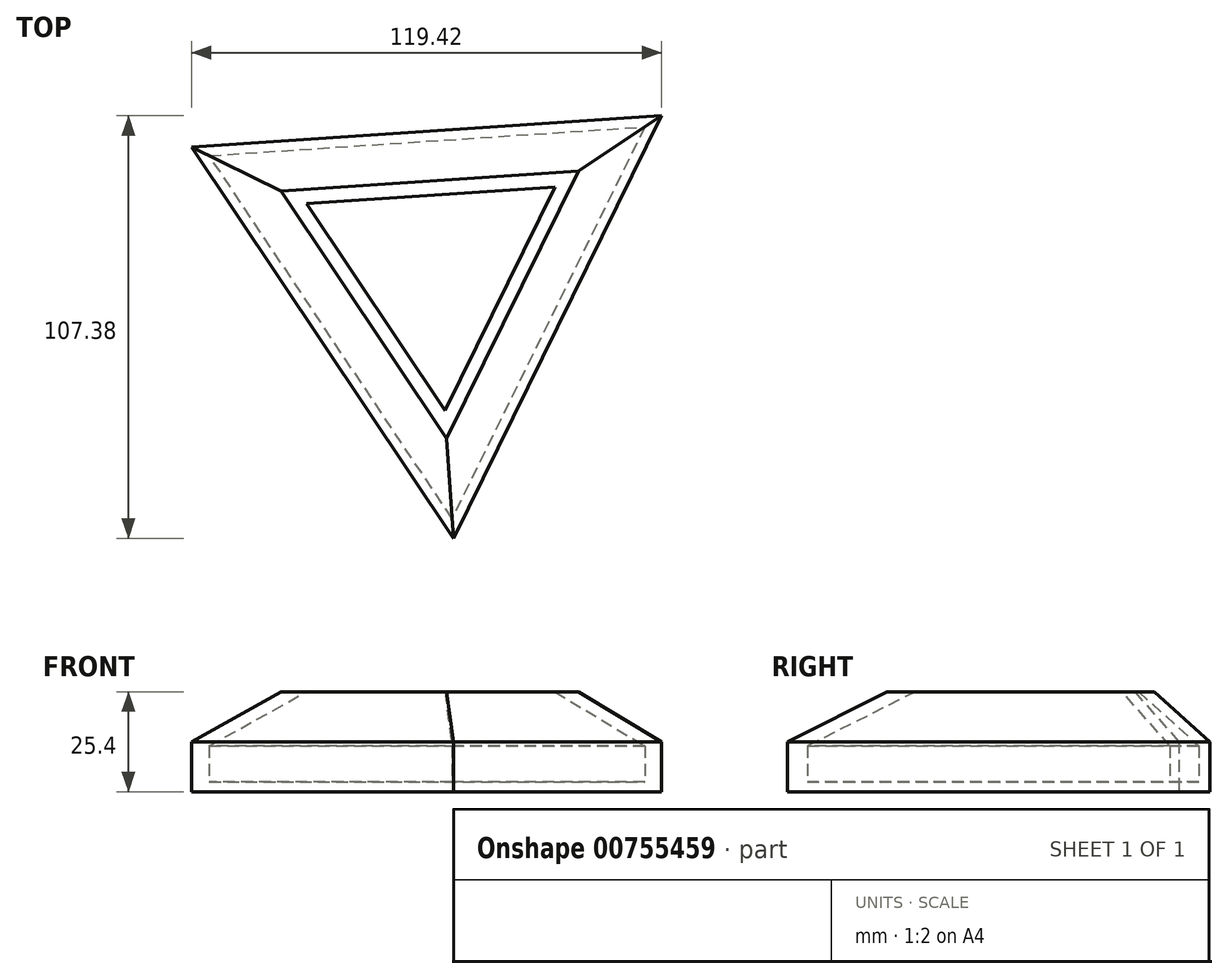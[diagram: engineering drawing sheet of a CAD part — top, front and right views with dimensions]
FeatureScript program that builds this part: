
annotation { "Feature Type Name" : "Feature", "Feature Type Description" : "" }
export const myFeature = defineFeature(function(context is Context, id is Id, definition is map)
    precondition{}
    {
        {
            var Q0;
            Q0=qCreatedBy(makeId("Top.planeOp"),FACE);
            var sketch = newSketch(context, id + "F0", { "sketchPlane" : qUnion([Q0])});
            skCircle(sketch, "E0.cCircle", {"center": v(0, 0) * mm, "radius": 34.55 * mm, "construction": true});
            skLineSegment(sketch, "E0.0", {"start": v(57.43, 38.43) * mm, "end": v(4.56, -68.95) * mm});
            skLineSegment(sketch, "E0.1", {"start": v(4.56, -68.95) * mm, "end": v(-62, 30.52) * mm});
            skLineSegment(sketch, "E0.2", {"start": v(-62, 30.52) * mm, "end": v(57.43, 38.43) * mm});
            skPoint(sketch, "E0.0.midPoint", {"position": v(31, -15.26) * mm});
            skSolve(sketch);
        }
        {
            var Q0;
            Q0=makeQuery(id+"F0.imprint","IMPRINT",FACE,{"disambiguationData":[TD([[makeQuery(id+"F0.imprint","IMPRINT",EDGE,{"derivedFrom":sQuery(id+"F0.wireOp",EDGE,"E0.0")}),-1.0]])]});
            extrude(context, id + "F1", {"entities" : qUnion([Q0]), "depth" : 25.4 * mm, "offsetDistance" : 25.4 * mm});
        }
        {
            var Q0;
            Q0=makeQuery(id+"F1.opExtrude","CAP_EDGE",EDGE,{"disambiguationData":[OSD([sQuery(id+"F0.wireOp",EDGE,"E0.0")])],"isStart":false});
            var Q1;
            Q1=makeQuery(id+"F1.opExtrude","CAP_EDGE",EDGE,{"disambiguationData":[OSD([sQuery(id+"F0.wireOp",EDGE,"E0.1")])],"isStart":false});
            var Q2;
            Q2=makeQuery(id+"F1.opExtrude","CAP_EDGE",EDGE,{"disambiguationData":[OSD([sQuery(id+"F0.wireOp",EDGE,"E0.2")])],"isStart":false});
            chamfer(context, id + "F2", {"entities" : qUnion([Q0, Q1, Q2]), "width" : 12.7 * mm, "tangentPropagation" : true});
        }
        {
            var Q0;
            Q0=makeQuery(id+"F1.opExtrude","CAP_FACE",FACE,{"disambiguationData":[OSD([sQuery(id+"F0.wireOp",EDGE,"E0.0"),sQuery(id+"F0.wireOp",EDGE,"E0.1"),sQuery(id+"F0.wireOp",EDGE,"E0.2")])],"isStart":false});
            shell(context, id + "F3", {"entities" : qUnion([Q0]), "thickness" : 2.54 * mm});
        }
    });
